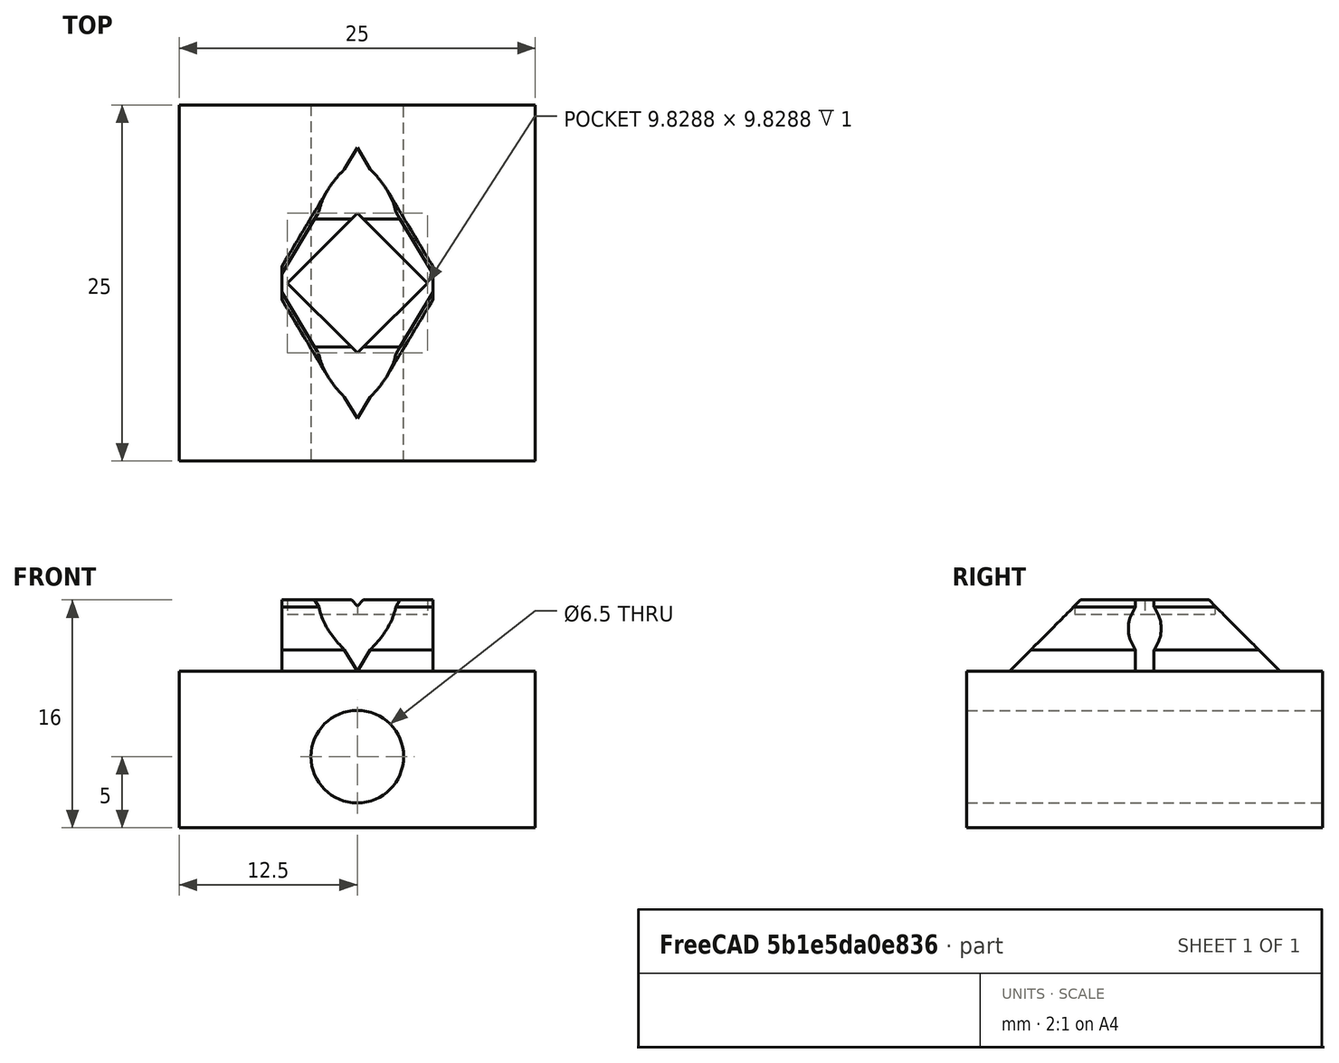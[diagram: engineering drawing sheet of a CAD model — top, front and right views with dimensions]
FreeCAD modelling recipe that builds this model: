
FCSTD DOCUMENT  (FreeCAD 1.1R20251031 (Git shallow))
Label: DockLink_application_example_assembly2
License: All rights reserved
LicenseURL: https://en.wikipedia.org/wiki/All_rights_reserved
objects: App::Link×2, App::Point×1, App::FeaturePython×1, Assembly::JointGroup×1, Part::MultiFuse×1, Assembly::AssemblyObject×1
note: 1 computed .brp shape members not serialized (recipe doc carries the construction recipe); baked Part::Feature solids carry a one-line shape summary decoded from their .brp
EXTERNAL_REF file=DockLink_application_example.FCStd obj=Body
EXTERNAL_REF file=DockLink_male.FCStd obj=Body

FEATURE [App::Point] Origin001
  Role = Origin
FEATURE [App::Link] DockLink_app_example
  LinkPlacement = pos=(-1.8e-15,-3.69549e-06,20) rot=(0,0,1;0rad)
  LinkedObject = -> <external DockLink_application_example.FCStd>#Body
  Placement = pos=(-1.8e-15,-3.69549e-06,20) rot=(0,0,1;0rad)
FEATURE [App::Link] Body_DockLink_male
  LinkPlacement = pos=(0,-3.69549e-06,31) rot=(0,0,1;0rad)
  LinkedObject = -> <external DockLink_male.FCStd>#Body
  Placement = pos=(0,-3.69549e-06,31) rot=(0,0,1;0rad)
FEATURE [App::FeaturePython] Joint  label="Fixed"  # Assembly joint (typed FeaturePython)
  Angle = 0
  AngleMax = 0
  AngleMin = 0
  Detach1 = false
  Detach2 = false
  Distance = 0
  Distance2 = 0
  EnableAngleMax = false
  EnableAngleMin = false
  EnableLengthMax = false
  EnableLengthMin = false
  JointType = 0 (Fixed)
  LengthMax = 0
  LengthMin = 0
  Placement1 = pos=(-12.5,0,10) rot=(-0.57735,-0.57735,0.57735;4.18879rad)
  Placement2 = pos=(-12.5,0,-1) rot=(-0.57735,-0.57735,0.57735;4.18879rad)
  Reference1 = -> Assembly [DockLink_app_example.Edge4,DockLink_app_example.Edge4]
  Reference2 = -> Assembly [Body_DockLink_male.Edge4,Body_DockLink_male.Edge4]
  Suppressed = false
FEATURE [Assembly::JointGroup] Joints
  Group = -> [Joint]
FEATURE [Part::MultiFuse] Fusion
  Refine = true
  Shapes = -> [DockLink_app_example,Body_DockLink_male]
FEATURE [Assembly::AssemblyObject] Assembly
  Group = -> [Joints,Joint,DockLink_app_example,Body_DockLink_male,Fusion]
  Origin = -> Origin
  Type = Assembly

RESOLVED EXTERNAL PARTS (link-assembly join: the EXTERNAL_REF files above that resolve inside this repo's crawl, each included once):
---- part DockLink_application_example.FCStd = doc fcstd_f1b1969aa827 ----
FCSTD DOCUMENT  (FreeCAD 1.1R20251031 (Git shallow))
Label: DockLink_application_example
License: All rights reserved
LicenseURL: https://en.wikipedia.org/wiki/All_rights_reserved
objects: Sketcher::SketchObject×2, App::Point×1, PartDesign::Pad×1, PartDesign::Pocket×1, PartDesign::Body×1
note: 11 computed .brp shape members not serialized (recipe doc carries the construction recipe); baked Part::Feature solids carry a one-line shape summary decoded from their .brp

FEATURE [App::Point] Origin001
  Role = Origin
FEATURE [Sketcher::SketchObject] Sketch
  ArcFitTolerance = 1e-06
  AttachmentSupport = -> [Origin]
  ExternalTypes = [0]
  FullyConstrained = true
  MakeInternals = false
  MapMode = 5
  sketch-geometry (5):
    g0: LineSegment StartX=-12.5 StartY=12.5 StartZ=0 EndX=-12.5 EndY=-12.5 EndZ=0
    g1: LineSegment StartX=-12.5 StartY=-12.5 StartZ=0 EndX=12.5 EndY=-12.5 EndZ=0
    g2: LineSegment StartX=12.5 StartY=-12.5 StartZ=0 EndX=12.5 EndY=12.5 EndZ=0
    g3: LineSegment StartX=12.5 StartY=12.5 StartZ=0 EndX=-12.5 EndY=12.5 EndZ=0
    g4: GeomPoint [constr] X=1e-16 Y=1e-16 Z=0
  constraints (12):
    c: Coincident(g0,g1)
    c: Coincident(g1,g2)
    c: Coincident(g2,g3)
    c: Coincident(g3,g0)
    c: Vertical(g0)
    c: Vertical(g2)
    c: Horizontal(g1)
    c: Horizontal(g3)
    c: Symmetric(g2,g0,g4)
    c: Coincident(g4,g-1)
    c: DistanceX(g3,g3) = 25
    c: Equal(g3,g0)
FEATURE [PartDesign::Pad] Pad
  Direction = (0,0,1)
  Length = 10
  Length2 = 10
  Profile = -> Sketch
  ReferenceAxis = -> Sketch [N_Axis]
  Refine = true
  SideType = 0
  Suppressed = false
  Type = 0
  Type2 = 0
FEATURE [Sketcher::SketchObject] Sketch001
  ArcFitTolerance = 1e-06
  AttachmentSupport = -> [Pad]
  ExternalGeometry = -> [Pad]
  ExternalTypes = [0,0]
  FullyConstrained = true
  MakeInternals = false
  MapMode = 5
  Placement = pos=(0,12.5,0) rot=(0,0.707107,0.707107;3.14159rad)
  sketch-geometry (2):
    g0: Circle CenterX=-1e-16 CenterY=5 CenterZ=0 NormalX=0 NormalY=0 NormalZ=1 AngleXU=0 Radius=3.25
    g1: GeomPoint X=-3e-16 Y=10 Z=0
  constraints (3):
    c: Symmetric(g-3,g-3,g1)
    c: Symmetric(g-1,g1,g0)
    c: Diameter(g0) = 6.5
FEATURE [PartDesign::Pocket] Pocket
  BaseFeature = -> Pad
  Direction = (0,-1,0)
  Length = 5
  Length2 = 5
  Profile = -> Sketch001
  ReferenceAxis = -> Sketch001 [N_Axis]
  Refine = true
  SideType = 0
  Suppressed = false
  Type = 1
  Type2 = 0
FEATURE [PartDesign::Body] Body  label="DockLink_app_example"
  AllowCompound = true
  Group = -> [Sketch,Pad,Sketch001,Pocket]
  Origin = -> Origin
  Tip = -> Pocket
---- part DockLink_male.FCStd = doc fcstd_4d2ef619000e ----
FCSTD DOCUMENT  (FreeCAD 1.1R20251031 (Git shallow))
Label: DockLink_male
License: All rights reserved
LicenseURL: https://en.wikipedia.org/wiki/All_rights_reserved
objects: Sketcher::SketchObject×8, PartDesign::Pocket×3, PartDesign::Pad×2, App::Point×1, App::VarSet×1, PartDesign::AdditiveLoft×1, PartDesign::Body×1
note: 35 computed .brp shape members not serialized (recipe doc carries the construction recipe); baked Part::Feature solids carry a one-line shape summary decoded from their .brp
EXTERNAL_REF file=DockLink_female.FCStd obj=VarSet

FEATURE [App::Point] Origin001
  Role = Origin
FEATURE [Sketcher::SketchObject] Sketch  label="Sketch_Base"
  ArcFitTolerance = 1e-06
  AttachmentSupport = -> [Origin]
  ExternalTypes = [0]
  FullyConstrained = true
  MakeInternals = false
  MapMode = 5
  expr: Constraints[10] = <<DockLink_female>>#VarSet.width_printbase
  expr: Constraints[11] = <<DockLink_female>>#VarSet.width_printbase
  expr: Constraints[22] = <<DockLink_female>>#VarSet.border_vert
  expr: Constraints[23] = <<DockLink_female>>#VarSet.border_hori
  sketch-geometry (10):
    g0: LineSegment StartX=-12.5 StartY=12.5 StartZ=0 EndX=-12.5 EndY=-12.5 EndZ=0
    g1: LineSegment StartX=-12.5 StartY=-12.5 StartZ=0 EndX=12.5 EndY=-12.5 EndZ=0
    g2: LineSegment StartX=12.5 StartY=-12.5 StartZ=0 EndX=12.5 EndY=12.5 EndZ=0
    g3: LineSegment StartX=12.5 StartY=12.5 StartZ=0 EndX=-12.5 EndY=12.5 EndZ=0
    g4: GeomPoint [constr] X=0 Y=0 Z=0
    g5: LineSegment [constr] StartX=-8.5 StartY=9.5 StartZ=0 EndX=-8.5 EndY=-9.5 EndZ=0
    g6: LineSegment [constr] StartX=-8.5 StartY=-9.5 StartZ=0 EndX=8.5 EndY=-9.5 EndZ=0
    g7: LineSegment [constr] StartX=8.5 StartY=-9.5 StartZ=0 EndX=8.5 EndY=9.5 EndZ=0
    g8: LineSegment [constr] StartX=8.5 StartY=9.5 StartZ=0 EndX=-8.5 EndY=9.5 EndZ=0
    g9: GeomPoint [constr] X=0 Y=0 Z=0
  constraints (24):
    c: Coincident(g0,g1)
    c: Coincident(g1,g2)
    c: Coincident(g2,g3)
    c: Coincident(g3,g0)
    c: Vertical(g0)
    c: Vertical(g2)
    c: Horizontal(g1)
    c: Horizontal(g3)
    c: Symmetric(g2,g0,g4)
    c: Coincident(g4,g-1)
    c: DistanceX(g3,g3) = 25
    c: DistanceY(g0,g0) = 25
    c: Coincident(g5,g6)
    c: Coincident(g6,g7)
    c: Coincident(g7,g8)
    c: Coincident(g8,g5)
    c: Vertical(g5)
    c: Vertical(g7)
    c: Horizontal(g6)
    c: Horizontal(g8)
    c: Symmetric(g7,g5,g9)
    c: Coincident(g9,g4)
    c: Distance(g3,g8) = 3
    c: Distance(g2,g7) = 4
FEATURE [App::VarSet] VarSet
  diameter_feet = 6.35
  feet_gap = 0.3
  thickness_base = 6
FEATURE [PartDesign::Pad] Pad  label="Pad_Base"
  Direction = (0,0,1)
  Length = 6
  Length2 = 10
  Profile = -> Sketch
  ReferenceAxis = -> Sketch [N_Axis]
  Refine = true
  Reversed = true
  SideType = 0
  Suppressed = false
  Type = 0
  Type2 = 0
  expr: Length = VarSet.thickness_base
FEATURE [Sketcher::SketchObject] Sketch001  label="Sketch_stud"
  ArcFitTolerance = 1e-06
  AttachmentSupport = -> [Pad]
  ExternalGeometry = -> [Pad]
  ExternalTypes = [0,0,0,0]
  FullyConstrained = true
  MakeInternals = false
  MapMode = 5
  expr: Constraints[18] = <<DockLink_female>>#VarSet.width_printbase - 2 * (<<DockLink_female>>#VarSet.border_hori + <<DockLink_female>>#VarSet.thickness_clip + <<DockLink_female>>#VarSet.indent_depth_clip + 0.5 mm)
  expr: Constraints[19] = <<DockLink_female>>#VarSet.border_vert
  sketch-geometry (8):
    g0: LineSegment [constr] StartX=-12.5 StartY=12.5 StartZ=0 EndX=-12.5 EndY=-12.5 EndZ=0
    g1: LineSegment [constr] StartX=-12.5 StartY=-12.5 StartZ=0 EndX=12.5 EndY=-12.5 EndZ=0
    g2: LineSegment [constr] StartX=12.5 StartY=-12.5 StartZ=0 EndX=12.5 EndY=12.5 EndZ=0
    g3: LineSegment [constr] StartX=12.5 StartY=12.5 StartZ=0 EndX=-12.5 EndY=12.5 EndZ=0
    g4: LineSegment StartX=0 StartY=9.5 StartZ=0 EndX=-5.7 EndY=0 EndZ=0
    g5: LineSegment StartX=-5.7 StartY=0 StartZ=0 EndX=0 EndY=-9.5 EndZ=0
    g6: LineSegment StartX=0 StartY=-9.5 StartZ=0 EndX=5.7 EndY=0 EndZ=0
    g7: LineSegment StartX=5.7 StartY=0 StartZ=0 EndX=0 EndY=9.5 EndZ=0
  constraints (20):
    c: Coincident(g0,g1)
    c: Coincident(g1,g2)
    c: Coincident(g2,g3)
    c: Coincident(g3,g0)
    c: Vertical(g0)
    c: Vertical(g2)
    c: Horizontal(g1)
    c: Horizontal(g3)
    c: Coincident(g0,g-3)
    c: Coincident(g1,g-4)
    c: PointOnObject(g4,g-2)
    c: PointOnObject(g4,g-1)
    c: Coincident(g5,g4)
    c: Coincident(g6,g5)
    c: Coincident(g7,g6)
    c: Coincident(g7,g4)
    c: Symmetric(g4,g5,g-1)
    c: Symmetric(g4,g6,g-1)
    c: Distance(g4,g6) = 11.4
    c: Distance(g4,g3) = 3
FEATURE [PartDesign::Pad] Pad001  label="Pad_stud"
  BaseFeature = -> Pad
  Direction = (0,0,1)
  Length = 5
  Length2 = 10
  Profile = -> Sketch001
  ReferenceAxis = -> Sketch001 [N_Axis]
  Refine = true
  SideType = 0
  Suppressed = false
  Type = 0
  Type2 = 0
  expr: Length = <<DockLink_female>>#VarSet.thickness_base - 1 mm
FEATURE [Sketcher::SketchObject] Sketch002  label="Sketch_nose_top"
  ArcFitTolerance = 1e-06
  AttachmentOffset = pos=(0,0,-0.5) rot=(0,0,1;0rad)
  AttachmentSupport = -> [Pad001]
  ExternalGeometry = -> [Pad001]
  ExternalTypes = [0,0,0,0]
  FullyConstrained = true
  MakeInternals = false
  MapMode = 5
  Placement = pos=(0,0,4.5) rot=(0,0,1;0rad)
  expr: .AttachmentOffset.Base.z = <<DockLink_female>>#VarSet.indent_distance - <<DockLink_female>>#VarSet.thickness_base + 1 mm + <<DockLink_female>>#VarSet.indent_height / 2
FEATURE [Sketcher::SketchObject] Sketch003  label="Sketch_nose_bottom"
  ArcFitTolerance = 1e-06
  AttachmentOffset = pos=(0,0,-3.5) rot=(0,0,1;0rad)
  AttachmentSupport = -> [Pad001]
  ExternalGeometry = -> [Pad001]
  ExternalTypes = [0,0,0,0]
  FullyConstrained = true
  MakeInternals = false
  MapMode = 5
  Placement = pos=(0,0,1.5) rot=(0,0,1;0rad)
  expr: .AttachmentOffset.Base.z = <<DockLink_female>>#VarSet.indent_distance - <<DockLink_female>>#VarSet.thickness_base + 1 mm - <<DockLink_female>>#VarSet.indent_height / 2
FEATURE [Sketcher::SketchObject] Sketch004  label="Sketch_nose_middle"
  ArcFitTolerance = 1e-06
  AttachmentOffset = pos=(0,0,-2) rot=(0,0,1;0rad)
  AttachmentSupport = -> [Pad001]
  ExternalGeometry = -> [Pad001]
  ExternalTypes = [0,0,0,0]
  FullyConstrained = true
  MakeInternals = false
  MapMode = 5
  Placement = pos=(0,0,3) rot=(0,0,1;0rad)
  expr: .AttachmentOffset.Base.z = <<DockLink_female>>#VarSet.indent_distance - <<DockLink_female>>#VarSet.thickness_base + 1 mm
  expr: Constraints[11] = DockLink_female#VarSet.indent_depth_clip
  sketch-geometry (4):
    g0: LineSegment StartX=0 StartY=10 StartZ=0 EndX=-6 EndY=0 EndZ=0
    g1: LineSegment StartX=-6 StartY=0 StartZ=0 EndX=0 EndY=-10 EndZ=0
    g2: LineSegment StartX=0 StartY=-10 StartZ=0 EndX=6 EndY=0 EndZ=0
    g3: LineSegment StartX=6 StartY=0 StartZ=0 EndX=0 EndY=10 EndZ=0
  constraints (12):
    c: PointOnObject(g0,g-2)
    c: PointOnObject(g0,g-1)
    c: Coincident(g1,g0)
    c: PointOnObject(g1,g-2)
    c: Coincident(g2,g1)
    c: PointOnObject(g2,g-1)
    c: Coincident(g3,g2)
    c: Coincident(g3,g0)
    c: Parallel(g-3,g0)
    c: Parallel(g3,g-4)
    c: Parallel(g2,g-5)
    c: Distance(g0,g-6) = 0.3
FEATURE [PartDesign::AdditiveLoft] AdditiveLoft  label="AdditiveLoft_nose"
  BaseFeature = -> Pad001
  Closed = false
  Profile = -> Sketch002
  Refine = true
  Ruled = false
  Sections = -> [Sketch004,Sketch003]
  Suppressed = false
FEATURE [Sketcher::SketchObject] Sketch005  label="Sketch_feet_recess"
  ArcFitTolerance = 1e-06
  AttachmentSupport = -> [AdditiveLoft]
  ExternalTypes = [0]
  FullyConstrained = true
  MakeInternals = false
  MapMode = 5
  Placement = pos=(0,0,5) rot=(0,0,1;0rad)
  expr: Constraints[13] = VarSet.diameter_feet + 2 * VarSet.feet_gap
  sketch-geometry (5):
    g0: LineSegment StartX=0 StartY=-4.91439 StartZ=0 EndX=4.91439 EndY=9e-16 EndZ=0
    g1: LineSegment StartX=4.91439 StartY=9e-16 StartZ=0 EndX=9e-16 EndY=4.91439 EndZ=0
    g2: LineSegment StartX=9e-16 StartY=4.91439 StartZ=0 EndX=-4.91439 EndY=9e-16 EndZ=0
    g3: LineSegment StartX=-4.91439 StartY=9e-16 StartZ=0 EndX=0 EndY=-4.91439 EndZ=0
    g4: Circle [constr] CenterX=0 CenterY=0 CenterZ=0 NormalX=0 NormalY=0 NormalZ=1 AngleXU=0 Radius=4.91439
  constraints (14):
    c: Coincident(g0,g1)
    c: Coincident(g1,g2)
    c: Coincident(g2,g3)
    c: Coincident(g3,g0)
    c: Equal(g0,g1)
    c: Equal(g0,g2)
    c: Equal(g0,g3)
    c: PointOnObject(g0,g4)
    c: PointOnObject(g1,g4)
    c: PointOnObject(g2,g4)
    c: PointOnObject(g3,g4)
    c: Coincident(g4,g-1)
    c: PointOnObject(g3,g-2)
    c: Distance(g0,g2) = 6.95
FEATURE [PartDesign::Pocket] Pocket  label="Pocket_feet_recess"
  BaseFeature = -> AdditiveLoft
  Direction = (0,0,-1)
  Length = 1
  Length2 = 5
  Profile = -> Sketch005
  ReferenceAxis = -> Sketch005 [N_Axis]
  Refine = true
  SideType = 0
  Suppressed = false
  Type = 0
  Type2 = 0
FEATURE [Sketcher::SketchObject] Sketch006  label="Sketch_feet_slant"
  ArcFitTolerance = 1e-06
  AttachmentSupport = -> [Origin]
  ExternalGeometry = -> [Pocket]
  ExternalTypes = [0,0,0,0,0,0]
  FullyConstrained = true
  MakeInternals = false
  MapMode = 5
  Placement = pos=(0,0,0) rot=(0.57735,0.57735,0.57735;2.0944rad)
  expr: Constraints[20] = <<DockLink_female>>#VarSet.indent_depth_clip + 1 mm
  sketch-geometry (10):
    g0: LineSegment [constr] StartX=-9.5 StartY=1.5 StartZ=0 EndX=-9.5 EndY=5 EndZ=0
    g1: LineSegment [constr] StartX=9.5 StartY=1.5 StartZ=0 EndX=9.5 EndY=5 EndZ=0
    g2: LineSegment StartX=-10.8 StartY=0 StartZ=0 EndX=-10.8 EndY=5 EndZ=0
    g3: LineSegment StartX=-10.8 StartY=5 StartZ=0 EndX=-4.5 EndY=5 EndZ=0
    g4: LineSegment StartX=-4.5 StartY=5 StartZ=0 EndX=-9.5 EndY=0 EndZ=0
    g5: LineSegment StartX=-9.5 StartY=0 StartZ=0 EndX=-10.8 EndY=0 EndZ=0
    g6: LineSegment StartX=10.8 StartY=0 StartZ=0 EndX=10.8 EndY=5 EndZ=0
    g7: LineSegment StartX=10.8 StartY=5 StartZ=0 EndX=4.5 EndY=5 EndZ=0
    g8: LineSegment StartX=4.5 StartY=5 StartZ=0 EndX=9.5 EndY=0 EndZ=0
    g9: LineSegment StartX=9.5 StartY=0 StartZ=0 EndX=10.8 EndY=0 EndZ=0
  constraints (25):
    c: Coincident(g0,g-3)
    c: Coincident(g0,g-7)
    c: Coincident(g1,g-4)
    c: Coincident(g1,g-8)
    c: PointOnObject(g2,g-1)
    c: Vertical(g2)
    c: Coincident(g3,g2)
    c: Horizontal(g3)
    c: Coincident(g4,g3)
    c: Coincident(g4,g-3)
    c: Coincident(g5,g4)
    c: Coincident(g5,g2)
    c: PointOnObject(g6,g-1)
    c: Vertical(g6)
    c: Coincident(g7,g6)
    c: Horizontal(g7)
    c: Coincident(g8,g7)
    c: Coincident(g8,g-4)
    c: Coincident(g9,g8)
    c: Coincident(g9,g6)
    c: Distance(g0,g2) = 1.3
    c: Angle(g4,g0) = 0.785398
    c: PointOnObject(g0,g3)
    c: Equal(g3,g7)
    c: Symmetric(g3,g7,g-2)
FEATURE [PartDesign::Pocket] Pocket001
  BaseFeature = -> Pocket
  Direction = (-1,0,0)
  Length = 5
  Length2 = 5
  Profile = -> Sketch006
  ReferenceAxis = -> Sketch006 [N_Axis]
  Refine = true
  SideType = 2
  Suppressed = false
  Type = 1
  Type2 = 0
FEATURE [Sketcher::SketchObject] Sketch007
  ArcFitTolerance = 1e-06
  AttachmentSupport = -> [Pocket001]
  ExternalGeometry = -> [Pocket001]
  ExternalTypes = [0,0,0,0,0,0]
  FullyConstrained = true
  MakeInternals = false
  MapMode = 5
  sketch-geometry (6):
    g0: LineSegment StartX=-5.3072 StartY=11.5 StartZ=0 EndX=-5.3072 EndY=-11.5 EndZ=0
    g1: LineSegment StartX=-5.3072 StartY=-11.5 StartZ=0 EndX=5.3072 EndY=-11.5 EndZ=0
    g2: LineSegment StartX=5.3072 StartY=-11.5 StartZ=0 EndX=5.3072 EndY=11.5 EndZ=0
    g3: LineSegment StartX=5.3072 StartY=11.5 StartZ=0 EndX=-5.3072 EndY=11.5 EndZ=0
    g4: GeomPoint [constr] X=0 Y=0 Z=0
    g5: GeomPoint [constr] X=5.3072 Y=4e-16 Z=0
  constraints (13):
    c: Coincident(g0,g1)
    c: Coincident(g1,g2)
    c: Coincident(g2,g3)
    c: Coincident(g3,g0)
    c: Vertical(g0)
    c: Vertical(g2)
    c: Horizontal(g1)
    c: Horizontal(g3)
    c: Symmetric(g2,g0,g4)
    c: Coincident(g4,g-1)
    c: Distance(g-4,g3) = 1
    c: Symmetric(g-7,g-8,g5)
    c: PointOnObject(g5,g2)
FEATURE [PartDesign::Pocket] Pocket002
  BaseFeature = -> Pocket001
  Direction = (0,0,-1)
  Length = 5
  Length2 = 5
  Profile = -> Sketch007
  ReferenceAxis = -> Sketch007 [N_Axis]
  Refine = true
  Reversed = true
  SideType = 0
  Suppressed = false
  Type = 1
  Type2 = 0
FEATURE [PartDesign::Body] Body  label="Body_DockLink_male"
  AllowCompound = true
  Group = -> [Sketch,Pad,Sketch001,Pad001,Sketch004,Sketch002,Sketch003,AdditiveLoft,Sketch005,Pocket,Sketch006,Pocket001,Sketch007,Pocket002]
  Origin = -> Origin
  Tip = -> Pocket002
